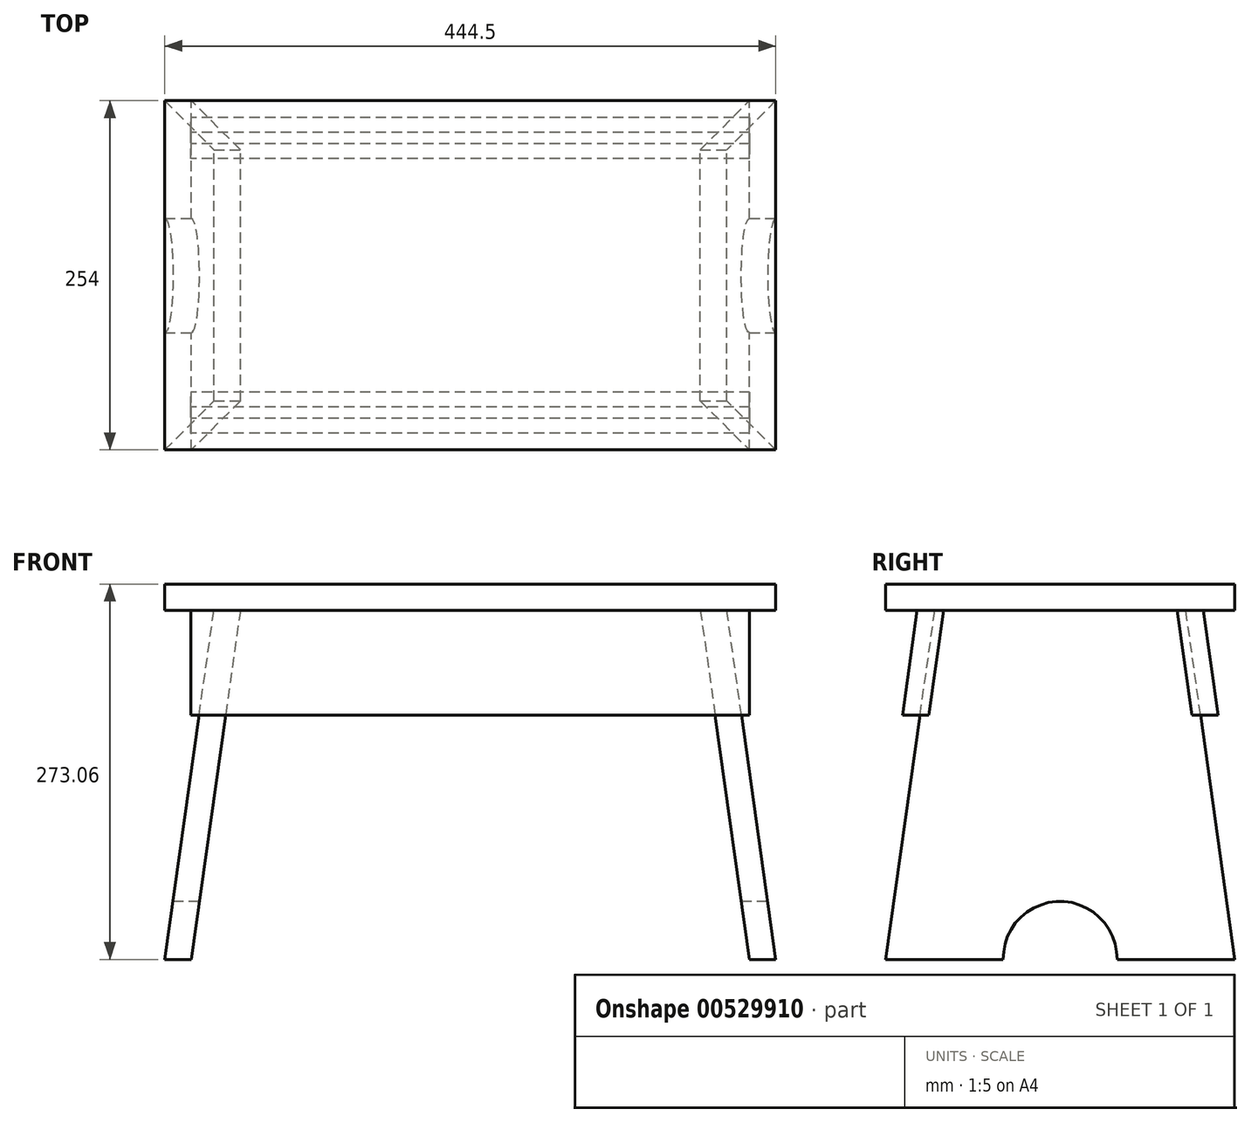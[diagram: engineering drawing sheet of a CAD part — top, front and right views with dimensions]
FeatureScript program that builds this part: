
annotation { "Feature Type Name" : "Feature", "Feature Type Description" : "" }
export const myFeature = defineFeature(function(context is Context, id is Id, definition is map)
    precondition{}
    {
        {
            var Q0;
            Q0=qCreatedBy(makeId("Front.planeOp"),FACE);
            var sketch = newSketch(context, id + "F0", { "sketchPlane" : qUnion([Q0])});
            skLineSegment(sketch, "E0.bottom", {"start": v(222.25, 9.53) * mm, "end": v(-222.25, 9.52) * mm});
            skLineSegment(sketch, "E0.top", {"start": v(222.25, -9.53) * mm, "end": v(-222.25, -9.53) * mm});
            skLineSegment(sketch, "E0.left", {"start": v(222.25, 9.53) * mm, "end": v(222.25, -9.52) * mm});
            skLineSegment(sketch, "E0.right", {"start": v(-222.25, 9.52) * mm, "end": v(-222.25, -9.53) * mm});
            skPoint(sketch, "E0.middle", {"position": v(0, 0) * mm});
            skLineSegment(sketch, "E1.bottom", {"start": v(-222.25, -9.53) * mm, "end": v(222.25, -9.53) * mm, "construction": true});
            skLineSegment(sketch, "E1.top", {"start": v(-222.25, -263.53) * mm, "end": v(222.25, -263.53) * mm, "construction": true});
            skLineSegment(sketch, "E1.left", {"start": v(-222.25, -9.53) * mm, "end": v(-222.25, -263.53) * mm, "construction": true});
            skLineSegment(sketch, "E1.right", {"start": v(222.25, -9.52) * mm, "end": v(222.25, -263.53) * mm, "construction": true});
            skLineSegment(sketch, "E2", {"start": v(186.55, -9.52) * mm, "end": v(222.25, -263.53) * mm});
            skLineSegment(sketch, "E3", {"start": v(203.01, -263.53) * mm, "end": v(167.32, -9.52) * mm});
            skLineSegment(sketch, "E4", {"start": v(-186.55, -9.53) * mm, "end": v(-222.25, -263.53) * mm});
            skLineSegment(sketch, "E5", {"start": v(-203.01, -263.53) * mm, "end": v(-167.32, -9.53) * mm});
            skLineSegment(sketch, "E6", {"start": v(-186.55, -9.53) * mm, "end": v(-167.32, -9.53) * mm});
            skLineSegment(sketch, "E7", {"start": v(167.32, -9.52) * mm, "end": v(186.55, -9.52) * mm});
            skLineSegment(sketch, "E8", {"start": v(0, 0) * mm, "end": v(0, -263.53) * mm, "construction": true});
            skLineSegment(sketch, "E9.bottom", {"start": v(-222.25, -9.53) * mm, "end": v(222.25, -9.53) * mm});
            skLineSegment(sketch, "E9.top", {"start": v(-222.25, -60.32) * mm, "end": v(222.25, -60.32) * mm});
            skLineSegment(sketch, "E9.left", {"start": v(-222.25, -9.53) * mm, "end": v(-222.25, -60.32) * mm});
            skLineSegment(sketch, "E9.right", {"start": v(222.25, -9.52) * mm, "end": v(222.25, -60.32) * mm});
            skLineSegment(sketch, "E10", {"start": v(200.83, -9.53) * mm, "end": v(193.7, -60.33) * mm});
            skLineSegment(sketch, "E11.MirrorCS", {"start": v(-200.83, -9.53) * mm, "end": v(-193.7, -60.33) * mm});
            skLineSegment(sketch, "E12", {"start": v(222.25, -263.53) * mm, "end": v(203.01, -263.53) * mm});
            skLineSegment(sketch, "E13", {"start": v(-222.25, -263.53) * mm, "end": v(-203.01, -263.53) * mm});
            skSolve(sketch);
        }
        {
            var Q0;
            Q0=makeQuery(id+"F0.imprint","IMPRINT",FACE,{"disambiguationData":[TD([[makeQuery(id+"F0.imprint","IMPRINT",EDGE,{"derivedFrom":sQuery(id+"F0.wireOp",EDGE,"E0.bottom")}),1.0]])]});
            extrude(context, id + "F1", {"entities" : qUnion([Q0]), "endBound" : BoundingType.SYMMETRIC, "depth" : 254 * mm, "offsetDistance" : 25.4 * mm});
        }
        {
            var Q0;
            {var subQ5=sQuery(id+"F0.wireOp",EDGE,"E9.bottom");var subQ6=sQuery(id+"F0.wireOp",EDGE,"E4");var subQ7=makeQuery(id+"F0.imprint","INTERSECT",VERTEX,{"derivedFrom":[subQ6,subQ5]});Q0=makeQuery(id+"F0.imprint","IMPRINT",FACE,{"disambiguationData":[TD([[makeQuery(id+"F0.imprint","IMPRINT",EDGE,{"disambiguationData":[TD([[subQ7,-1.0]])],"derivedFrom":subQ6}),1.0]])]});}
            var Q1;
            {var subQ0=sQuery(id+"F0.wireOp",EDGE,"E9.bottom");var subQ5=sQuery(id+"F0.wireOp",EDGE,"E3");var subQ6=makeQuery(id+"F0.imprint","INTERSECT",VERTEX,{"derivedFrom":[subQ5,subQ0]});Q1=makeQuery(id+"F0.imprint","IMPRINT",FACE,{"disambiguationData":[TD([[makeQuery(id+"F0.imprint","IMPRINT",EDGE,{"disambiguationData":[TD([[subQ6,1.0]])],"derivedFrom":subQ5}),-1.0]])]});}
            var Q2;
            {var subQ6=sQuery(id+"F0.wireOp",EDGE,"E13");Q2=makeQuery(id+"F0.imprint","IMPRINT",FACE,{"disambiguationData":[TD([[makeQuery(id+"F0.imprint","IMPRINT",EDGE,{"derivedFrom":subQ6}),1.0]])]});}
            var Q3;
            {var subQ0=sQuery(id+"F0.wireOp",EDGE,"E12");Q3=makeQuery(id+"F0.imprint","IMPRINT",FACE,{"disambiguationData":[TD([[makeQuery(id+"F0.imprint","IMPRINT",EDGE,{"derivedFrom":subQ0}),-1.0]])]});}
            var Q4;
            Q4=makeQuery(id+"F1.opExtrude","CAP_VERTEX",VERTEX,{"disambiguationData":[OSD([sQuery(id+"F0.wireOp",EDGE,"E0.left"),sQuery(id+"F0.wireOp",EDGE,"E9.bottom")])],"isStart":false});
            var Q5;
            Q5=makeQuery(id+"F1.opExtrude","CAP_VERTEX",VERTEX,{"disambiguationData":[OSD([sQuery(id+"F0.wireOp",EDGE,"E0.left"),sQuery(id+"F0.wireOp",EDGE,"E9.bottom")])],"isStart":true});
            extrude(context, id + "F2", {"entities" : qUnion([Q0, Q1, Q2, Q3]), "endBound" : BoundingType.UP_TO_VERTEX, "depth" : 228.6 * mm, "endBoundEntityVertex" : qUnion([Q4]), "offsetDistance" : 25.4 * mm, "hasSecondDirection" : true, "secondDirectionBound" : SecondDirectionBoundingType.UP_TO_VERTEX, "secondDirectionOppositeDirection" : true, "secondDirectionDepth" : 25.4 * mm, "secondDirectionBoundEntityVertex" : qUnion([Q5])});
        }
        {
            var Q0;
            Q0=qCreatedBy(makeId("Right.planeOp"),FACE);
            var sketch = newSketch(context, id + "F3", { "sketchPlane" : qUnion([Q0])});
            skLineSegment(sketch, "E14.0.0", {"start": v(127, -9.53) * mm, "end": v(-127, -9.53) * mm});
            skLineSegment(sketch, "E14.0.1", {"start": v(-127, -9.53) * mm, "end": v(-127, -263.53) * mm});
            skLineSegment(sketch, "E14.0.2", {"start": v(-127, -263.53) * mm, "end": v(127, -263.53) * mm});
            skLineSegment(sketch, "E14.0.3", {"start": v(127, -263.53) * mm, "end": v(127, -9.53) * mm});
            skLineSegment(sketch, "E15", {"start": v(-127, -263.53) * mm, "end": v(-91.3, -9.53) * mm});
            skArc(sketch, "E16", {"start": v(41.34, -263.53) * mm, "mid": v(-0.23, -221.22) * mm, "end": v(-41.79, -263.53) * mm});
            skLineSegment(sketch, "E17", {"start": v(0, -263.53) * mm, "end": v(0, -297.02) * mm, "construction": true});
            skLineSegment(sketch, "E18", {"start": v(127, -263.53) * mm, "end": v(91.3, -9.53) * mm});
            skSolve(sketch);
        }
        {
            var Q0;
            {var subQ0=sQuery(id+"F3.wireOp",EDGE,"E14.0.1");Q0=makeQuery(id+"F3.imprint","IMPRINT",FACE,{"disambiguationData":[TD([[makeQuery(id+"F3.imprint","IMPRINT",EDGE,{"derivedFrom":subQ0}),1.0]])]});}
            var Q1;
            {var subQ0=sQuery(id+"F3.wireOp",EDGE,"E16");Q1=makeQuery(id+"F3.imprint","IMPRINT",FACE,{"disambiguationData":[TD([[makeQuery(id+"F3.imprint","IMPRINT",EDGE,{"derivedFrom":subQ0}),1.0]])]});}
            var Q2;
            {var subQ0=sQuery(id+"F3.wireOp",EDGE,"E14.0.3");Q2=makeQuery(id+"F3.imprint","IMPRINT",FACE,{"disambiguationData":[TD([[makeQuery(id+"F3.imprint","IMPRINT",EDGE,{"derivedFrom":subQ0}),1.0]])]});}
            extrude(context, id + "F4", {"entities" : qUnion([Q0, Q1, Q2]), "operationType" : NewBodyOperationType.REMOVE, "endBound" : BoundingType.THROUGH_ALL, "oppositeDirection" : true, "depth" : 25.4 * mm, "offsetDistance" : 25.4 * mm, "hasSecondDirection" : true, "secondDirectionBound" : SecondDirectionBoundingType.THROUGH_ALL, "secondDirectionOppositeDirection" : false, "secondDirectionDepth" : 25.4 * mm});
        }
        {
            var Q0;
            Q0=qCreatedBy(makeId("Right.planeOp"),FACE);
            var sketch = newSketch(context, id + "F5", { "sketchPlane" : qUnion([Q0])});
            skLineSegment(sketch, "E19", {"start": v(-104.13, -9.53) * mm, "end": v(-114.84, -85.73) * mm});
            skLineSegment(sketch, "E20", {"start": v(-114.84, -85.72) * mm, "end": v(-95.6, -85.72) * mm});
            skLineSegment(sketch, "E21", {"start": v(-95.6, -85.72) * mm, "end": v(-84.9, -9.52) * mm});
            skLineSegment(sketch, "E22", {"start": v(-84.9, -9.53) * mm, "end": v(-104.13, -9.53) * mm});
            skLineSegment(sketch, "E23.MirrorCS", {"start": v(95.6, -85.73) * mm, "end": v(84.9, -9.52) * mm});
            skLineSegment(sketch, "E24.MirrorCS", {"start": v(84.9, -9.53) * mm, "end": v(104.13, -9.53) * mm});
            skLineSegment(sketch, "E25.MirrorCS", {"start": v(104.13, -9.52) * mm, "end": v(114.84, -85.72) * mm});
            skLineSegment(sketch, "E26.MirrorCS", {"start": v(114.84, -85.73) * mm, "end": v(95.6, -85.73) * mm});
            skLineSegment(sketch, "E27.0.0", {"start": v(-91.3, -9.53) * mm, "end": v(-127, -263.53) * mm, "construction": true});
            skLineSegment(sketch, "E27.0.1", {"start": v(-127, -263.53) * mm, "end": v(-41.79, -263.53) * mm, "construction": true});
            skArc(sketch, "E27.0.2", {"start": v(-41.79, -263.53) * mm, "mid": v(-0.23, -221.22) * mm, "end": v(41.34, -263.53) * mm, "construction": true});
            skLineSegment(sketch, "E27.0.3", {"start": v(41.34, -263.53) * mm, "end": v(127, -263.53) * mm, "construction": true});
            skLineSegment(sketch, "E27.0.4", {"start": v(127, -263.53) * mm, "end": v(91.3, -9.52) * mm, "construction": true});
            skLineSegment(sketch, "E27.0.5", {"start": v(91.3, -9.53) * mm, "end": v(-91.3, -9.53) * mm, "construction": true});
            skLineSegment(sketch, "E28.0.0", {"start": v(91.3, -9.52) * mm, "end": v(127, -263.53) * mm, "construction": true});
            skLineSegment(sketch, "E28.0.1", {"start": v(127, -263.53) * mm, "end": v(127, -9.53) * mm, "construction": true});
            skLineSegment(sketch, "E28.0.2", {"start": v(127, -9.53) * mm, "end": v(91.3, -9.53) * mm, "construction": true});
            skSolve(sketch);
        }
        {
            var Q0;
            Q0=makeQuery(id+"F5.imprint","IMPRINT",FACE,{"disambiguationData":[TD([[makeQuery(id+"F5.imprint","IMPRINT",EDGE,{"derivedFrom":sQuery(id+"F5.wireOp",EDGE,"E19")}),1.0]])]});
            var Q1;
            Q1=makeQuery(id+"F5.imprint","IMPRINT",FACE,{"disambiguationData":[TD([[makeQuery(id+"F5.imprint","IMPRINT",EDGE,{"derivedFrom":sQuery(id+"F5.wireOp",EDGE,"E23.MirrorCS")}),-1.0]])]});
            extrude(context, id + "F6", {"entities" : qUnion([Q0, Q1]), "endBound" : BoundingType.SYMMETRIC, "depth" : 406.4 * mm, "offsetDistance" : 25.4 * mm});
        }
    });
